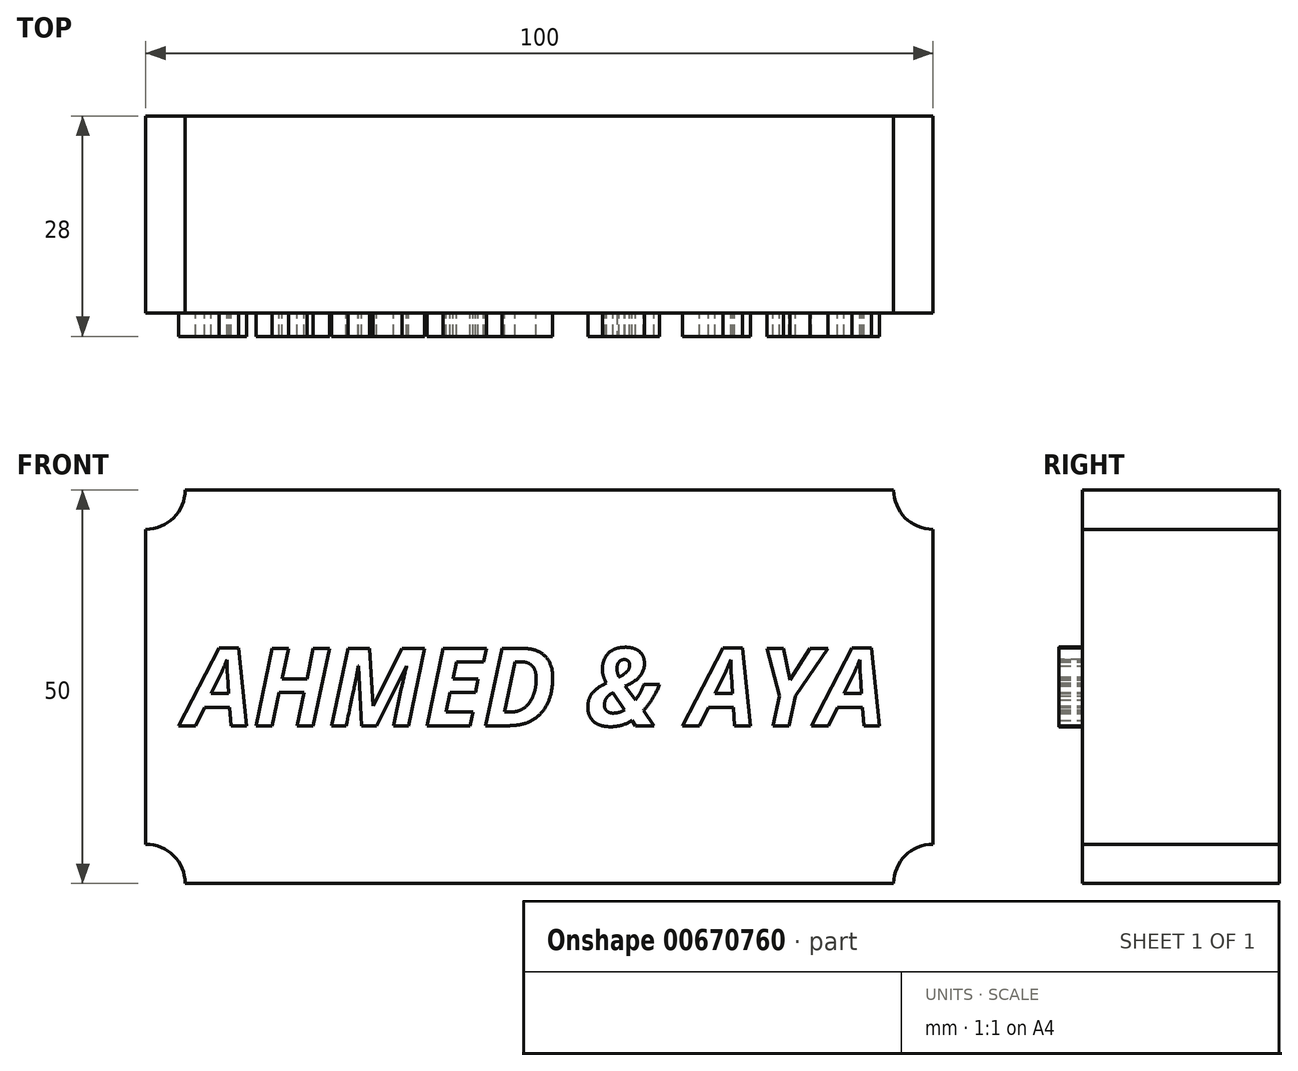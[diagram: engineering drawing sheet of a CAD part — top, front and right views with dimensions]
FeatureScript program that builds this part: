
annotation { "Feature Type Name" : "Feature", "Feature Type Description" : "" }
export const myFeature = defineFeature(function(context is Context, id is Id, definition is map)
    precondition{}
    {
        {
            var Q0;
            Q0=qCreatedBy(makeId("Front.planeOp"),FACE);
            var sketch = newSketch(context, id + "F0", { "sketchPlane" : qUnion([Q0])});
            skLineSegment(sketch, "E0.bottom", {"start": v(45, 25) * mm, "end": v(-45, 25) * mm});
            skLineSegment(sketch, "E0.top", {"start": v(45, -25) * mm, "end": v(-45, -25) * mm});
            skLineSegment(sketch, "E0.left", {"start": v(50, 20) * mm, "end": v(50, -20) * mm});
            skLineSegment(sketch, "E0.right", {"start": v(-50, 20) * mm, "end": v(-50, -20) * mm});
            skPoint(sketch, "E0.middle", {"position": v(0, 0) * mm});
            skArc(sketch, "E1", {"start": v(45, 25) * mm, "mid": v(46.46, 21.46) * mm, "end": v(50, 20) * mm});
            skArc(sketch, "E2", {"start": v(-50, 20) * mm, "mid": v(-46.46, 21.46) * mm, "end": v(-45, 25) * mm});
            skArc(sketch, "E3", {"start": v(50, -20) * mm, "mid": v(46.46, -21.46) * mm, "end": v(45, -25) * mm});
            skArc(sketch, "E4", {"start": v(-45, -25) * mm, "mid": v(-46.46, -21.46) * mm, "end": v(-50, -20) * mm});
            skSolve(sketch);
        }
        {
            var Q0;
            Q0 = qSketchRegion(id + "F0", true);
            extrude(context, id + "F1", {"entities" : qUnion([Q0]), "oppositeDirection" : true, "depth" : 25 * mm, "offsetDistance" : 25 * mm});
        }
        {
            var Q0;
            Q0=qCreatedBy(makeId("Front.planeOp"),FACE);
            var sketch = newSketch(context, id + "F2", { "sketchPlane" : qUnion([Q0])});
            skText(sketch, "E5", { "text": "AHMED & AYA", "fontName": "OpenSans-BoldItalic.ttf"});
            const initialGuessF2  = {"E5": [-0.045, -0.00495, 1, 0, 0.0099]};
            skSetInitialGuess(sketch, initialGuessF2);
            skSolve(sketch);
        }
        {
            var Q0;
            Q0 = qSketchRegion(id + "F2", true);
            extrude(context, id + "F3", {"entities" : qUnion([Q0]), "operationType" : NewBodyOperationType.ADD, "depth" : 3 * mm, "offsetDistance" : 25 * mm});
        }
    });
